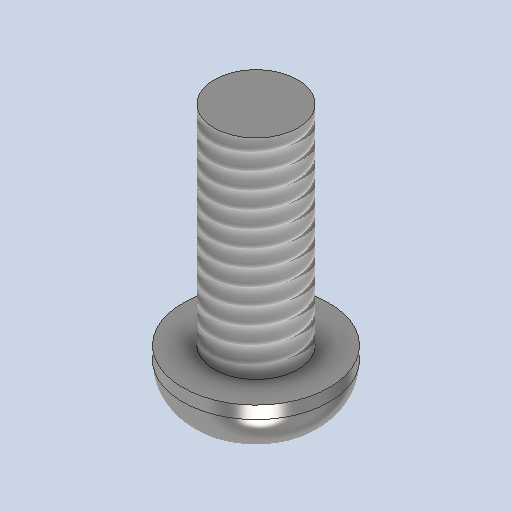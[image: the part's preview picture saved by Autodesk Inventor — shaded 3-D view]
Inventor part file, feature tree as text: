
AUTODESK INVENTOR PART (.ipt)
format: ipt  version: 2024.2 (Build 282272000, 272)  size: 228,864 bytes
history: native  units: mm
features: sketch x2, revolve x2, other x1, thread x1, extrude x1
ambient origin geometry x8: Origin, YZ Plane, XZ Plane, XY Plane, X Axis, Y Axis, Z Axis, Center Point
bodies: Body1 (feature_tree)
feature tree (7):
  other  "ソリッド1"
  sketch  "スケッチ1"
  revolve  "回転1"
  thread  "ねじ1"
  extrude  "押し出し2"  Depth=1.3mm
  revolve  "回転2"
  sketch  "スケッチ2"
